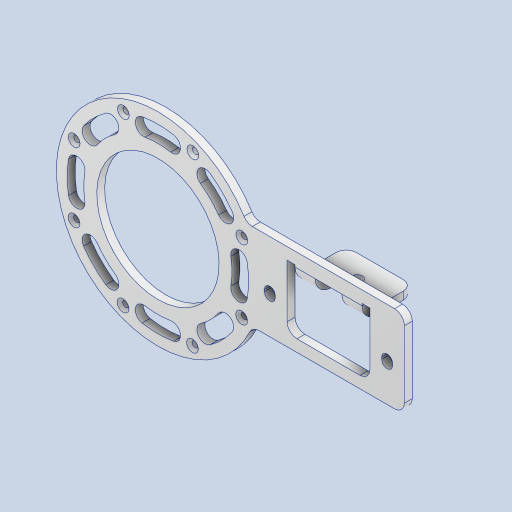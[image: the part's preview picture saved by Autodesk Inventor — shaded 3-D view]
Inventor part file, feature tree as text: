
AUTODESK INVENTOR PART (.ipt)
format: ipt  version: 2023 (Build 270158000, 158)  size: 1,512,448 bytes
history: native  units: mm
features: other x6, sketch x3, fillet x1, hole x1
ambient origin geometry x8: Origin, YZ Plane, XZ Plane, XY Plane, X Axis, Y Axis, Z Axis, Center Point
bodies: Body1 (feature_tree), Body2 (feature_tree)
feature tree (11):
  other  "GIM8108-8_1.ipt"
  other  "折り曲げ1"
  fillet  "フィレット1"  Radius=10.0mm
  hole  "穴1"  [1 undecoded]
  other  "TaggingFeature1"
  sketch  "スケッチ2"
  other  "プレート1"
  sketch  "スケッチ3"
  sketch  "スケッチ4"
  other  "ソリッド1::GIM8108-8_1.ipt"
  other  "Srf1"
note: 1 required parameter value undecoded (feature->parameter linkage not recoverable at this tier; creation-order binding heuristic only, values carry confidence <= 0.55)
